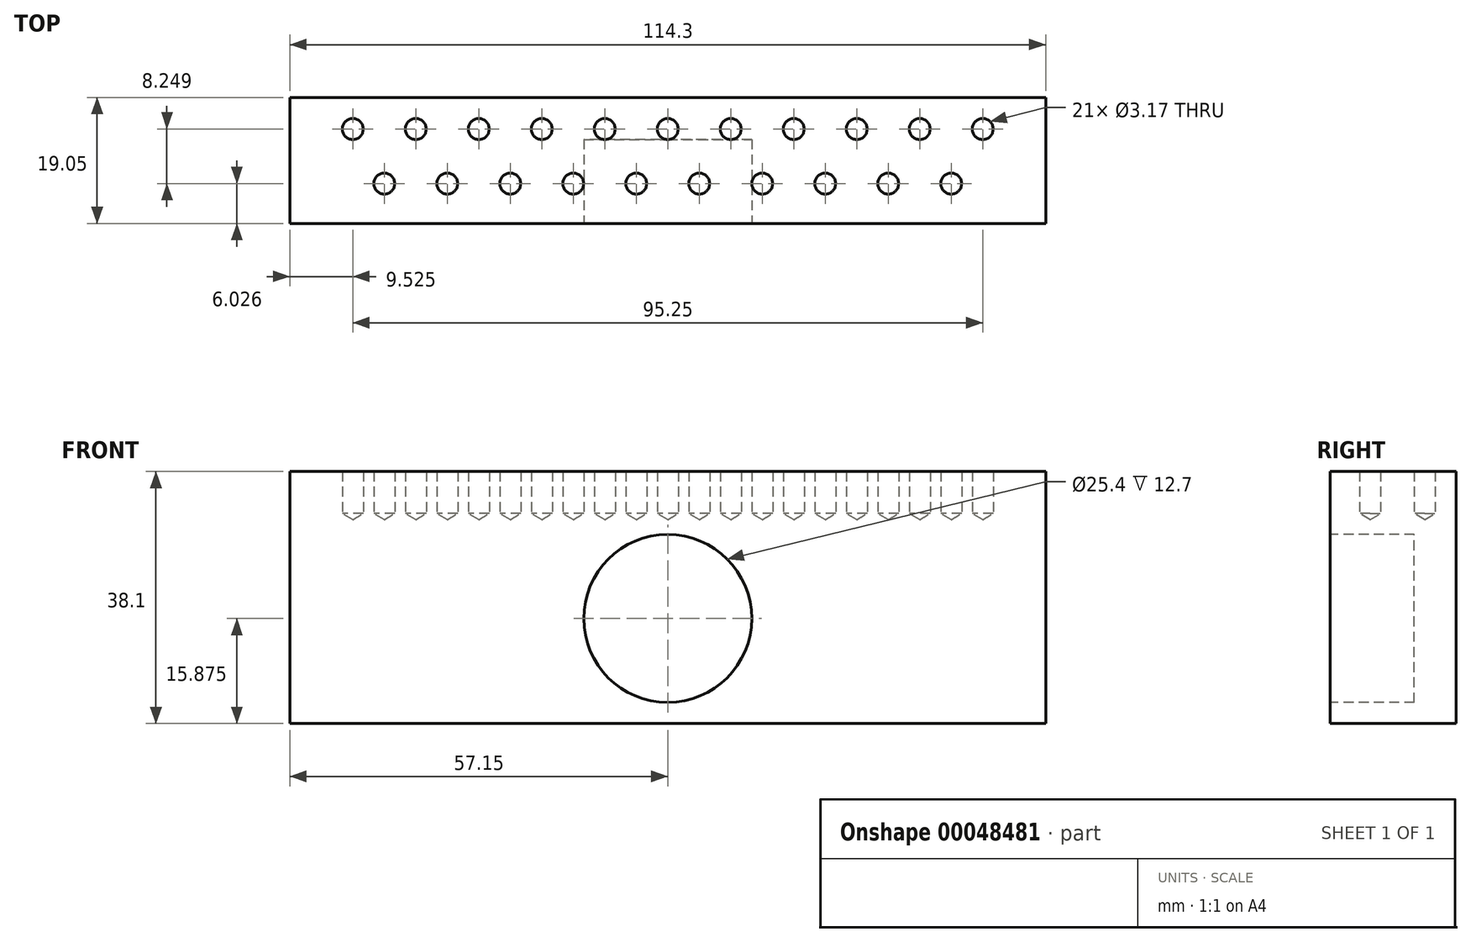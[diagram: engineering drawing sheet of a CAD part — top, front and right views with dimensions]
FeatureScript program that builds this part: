
annotation { "Feature Type Name" : "Feature", "Feature Type Description" : "" }
export const myFeature = defineFeature(function(context is Context, id is Id, definition is map)
    precondition{}
    {
        {
            var Q0;
            Q0=qCreatedBy(makeId("Right.planeOp"),FACE);
            var sketch = newSketch(context, id + "F0", { "sketchPlane" : qUnion([Q0])});
            skLineSegment(sketch, "E0.bottom", {"start": v(0, 0) * mm, "end": v(19.05, 0) * mm});
            skLineSegment(sketch, "E0.top", {"start": v(0, 38.1) * mm, "end": v(19.05, 38.1) * mm});
            skLineSegment(sketch, "E0.left", {"start": v(0, 0) * mm, "end": v(0, 38.1) * mm});
            skLineSegment(sketch, "E0.right", {"start": v(19.05, 0) * mm, "end": v(19.05, 38.1) * mm});
            skSolve(sketch);
        }
        {
            var Q0;
            Q0 = qSketchRegion(id + "F0", true);
            extrude(context, id + "F1", {"entities" : qUnion([Q0]), "depth" : 114.3 * mm, "symmetric" : true});
        }
        {
            var Q0;
            Q0=makeQuery(id+"F1.opExtrude","SWEPT_FACE",FACE,{"disambiguationData":[OSD([sQuery(id+"F0.wireOp",EDGE,"E0.left")])]});
            var sketch = newSketch(context, id + "F2", { "sketchPlane" : qUnion([Q0])});
            skCircle(sketch, "E1", {"center": v(0, 15.88) * mm, "radius": 12.7 * mm});
            skSolve(sketch);
        }
        {
            var Q0;
            Q0=makeQuery(id+"F2.imprint","IMPRINT",FACE,{"disambiguationData":[TD([[makeQuery(id+"F2.imprint","IMPRINT",EDGE,{"derivedFrom":sQuery(id+"F2.wireOp",EDGE,"E1")}),1.0]])]});
            var Q1;
            Q1=sQuery(id+"F2.wireOp",EDGE,"E1");
            extrude(context, id + "F3", {"entities" : qUnion([Q0]), "operationType" : NewBodyOperationType.REMOVE, "surfaceEntities" : qUnion([Q1]), "oppositeDirection" : true, "depth" : 12.7 * mm});
        }
        {
            var Q0;
            Q0=makeQuery(id+"F1.opExtrude","SWEPT_FACE",FACE,{"disambiguationData":[OSD([sQuery(id+"F0.wireOp",EDGE,"E0.top")])]});
            var sketch = newSketch(context, id + "F4", { "sketchPlane" : qUnion([Q0])});
            skPoint(sketch, "E2", {"position": v(-47.63, 14.27) * mm});
            skPoint(sketch, "E3.1.0.0", {"position": v(-38.1, 14.27) * mm});
            skPoint(sketch, "E3.2.0.0", {"position": v(-28.58, 14.27) * mm});
            skPoint(sketch, "E3.3.0.0", {"position": v(-19.05, 14.27) * mm});
            skPoint(sketch, "E3.4.0.0", {"position": v(-9.53, 14.27) * mm});
            skPoint(sketch, "E3.5.0.0", {"position": v(0, 14.27) * mm});
            skPoint(sketch, "E3.6.0.0", {"position": v(9.52, 14.27) * mm});
            skPoint(sketch, "E3.7.0.0", {"position": v(19.05, 14.27) * mm});
            skPoint(sketch, "E3.8.0.0", {"position": v(28.57, 14.27) * mm});
            skPoint(sketch, "E3.9.0.0", {"position": v(38.1, 14.27) * mm});
            skPoint(sketch, "E3.10.0.0", {"position": v(47.62, 14.27) * mm});
            skLineSegment(sketch, "E3.direction1", {"start": v(-47.63, 14.27) * mm, "end": v(-38.1, 14.27) * mm, "construction": true});
            skPoint(sketch, "E4", {"position": v(-42.86, 6.03) * mm});
            skPoint(sketch, "E5.1.0.0", {"position": v(-33.34, 6.03) * mm});
            skPoint(sketch, "E5.2.0.0", {"position": v(-23.81, 6.03) * mm});
            skPoint(sketch, "E5.3.0.0", {"position": v(-14.29, 6.03) * mm});
            skPoint(sketch, "E5.4.0.0", {"position": v(-4.76, 6.03) * mm});
            skPoint(sketch, "E5.5.0.0", {"position": v(4.76, 6.03) * mm});
            skPoint(sketch, "E5.6.0.0", {"position": v(14.29, 6.03) * mm});
            skPoint(sketch, "E5.7.0.0", {"position": v(23.81, 6.03) * mm});
            skPoint(sketch, "E5.8.0.0", {"position": v(33.34, 6.03) * mm});
            skPoint(sketch, "E5.9.0.0", {"position": v(42.86, 6.03) * mm});
            skLineSegment(sketch, "E5.direction1", {"start": v(-42.86, 6.03) * mm, "end": v(-33.34, 6.03) * mm, "construction": true});
            skSolve(sketch);
        }
        {
            var Q0;
            Q0=sQuery(id+"F4.wireOp",VERTEX,"E3.5.0.0");
            var Q1;
            Q1=sQuery(id+"F4.wireOp",VERTEX,"E2");
            var Q2;
            Q2=sQuery(id+"F4.wireOp",VERTEX,"E5.3.0.0");
            var Q3;
            Q3=sQuery(id+"F4.wireOp",VERTEX,"E5.2.0.0");
            var Q4;
            Q4=sQuery(id+"F4.wireOp",VERTEX,"E5.7.0.0");
            var Q5;
            Q5=sQuery(id+"F4.wireOp",VERTEX,"E5.1.0.0");
            var Q6;
            Q6=sQuery(id+"F4.wireOp",VERTEX,"E3.8.0.0");
            var Q7;
            Q7=sQuery(id+"F4.wireOp",VERTEX,"E5.5.0.0");
            var Q8;
            Q8=sQuery(id+"F4.wireOp",VERTEX,"E5.4.0.0");
            var Q9;
            Q9=sQuery(id+"F4.wireOp",VERTEX,"E3.3.0.0");
            var Q10;
            Q10=sQuery(id+"F4.wireOp",VERTEX,"E5.6.0.0");
            var Q11;
            Q11=sQuery(id+"F4.wireOp",VERTEX,"E3.6.0.0");
            var Q12;
            Q12=sQuery(id+"F4.wireOp",VERTEX,"E3.7.0.0");
            var Q13;
            Q13=sQuery(id+"F4.wireOp",VERTEX,"E5.9.0.0");
            var Q14;
            Q14=sQuery(id+"F4.wireOp",VERTEX,"E5.8.0.0");
            var Q15;
            Q15=sQuery(id+"F4.wireOp",VERTEX,"E3.10.0.0");
            var Q16;
            Q16=sQuery(id+"F4.wireOp",VERTEX,"E4");
            var Q17;
            Q17=sQuery(id+"F4.wireOp",VERTEX,"E3.9.0.0");
            var Q18;
            Q18=sQuery(id+"F4.wireOp",VERTEX,"E3.2.0.0");
            var Q19;
            Q19=sQuery(id+"F4.wireOp",VERTEX,"E3.4.0.0");
            var Q20;
            Q20=sQuery(id+"F4.wireOp",VERTEX,"E3.1.0.0");
            var Q21;
            Q21=makeQuery(id+"F1.opExtrude","SWEPT_BODY",BODY,{"disambiguationData":[OSD([sQuery(id+"F0.wireOp",EDGE,"E0.bottom"),sQuery(id+"F0.wireOp",EDGE,"E0.top"),sQuery(id+"F0.wireOp",EDGE,"E0.left"),sQuery(id+"F0.wireOp",EDGE,"E0.right")])]});
            hole(context, id + "F5", {"style" : HoleStyle.SIMPLE, "holeDiameter" : 3.17 * mm, "endStyle" : HoleEndStyle.BLIND, "holeDepth" : 6.35 * mm, "locations" : qUnion([Q0, Q1, Q2, Q3, Q4, Q5, Q6, Q7, Q8, Q9, Q10, Q11, Q12, Q13, Q14, Q15, Q16, Q17, Q18, Q19, Q20]), "scope" : qUnion([Q21])});
        }
    });
